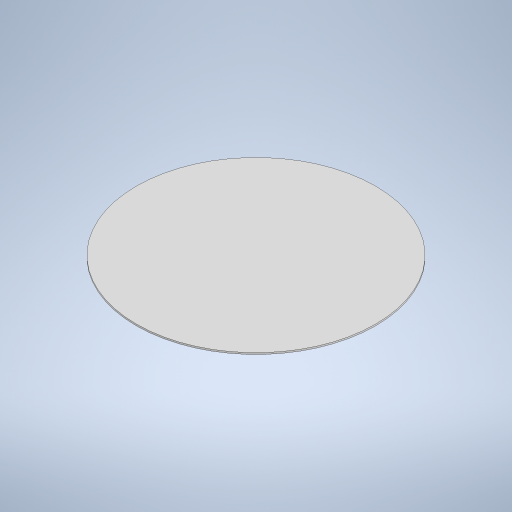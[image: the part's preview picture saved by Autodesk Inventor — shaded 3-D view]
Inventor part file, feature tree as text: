
AUTODESK INVENTOR PART (.ipt)
format: ipt  version: 2024.2 (Build 282272000, 272)  size: 206,336 bytes
history: native  units: mm
features: extrude x1, sketch x1
ambient origin geometry x8: Origin, YZ Plane, XZ Plane, XY Plane, X Axis, Y Axis, Z Axis, Center Point
bodies: Solid1 (feature_tree)
feature tree (2):
  extrude  "Extrusion1"  Depth=3.0mm TaperAngle=0.0deg
  sketch  "Sketch1"  dims[d0=450.0mm d1=3.0mm d2=0.0mm]
